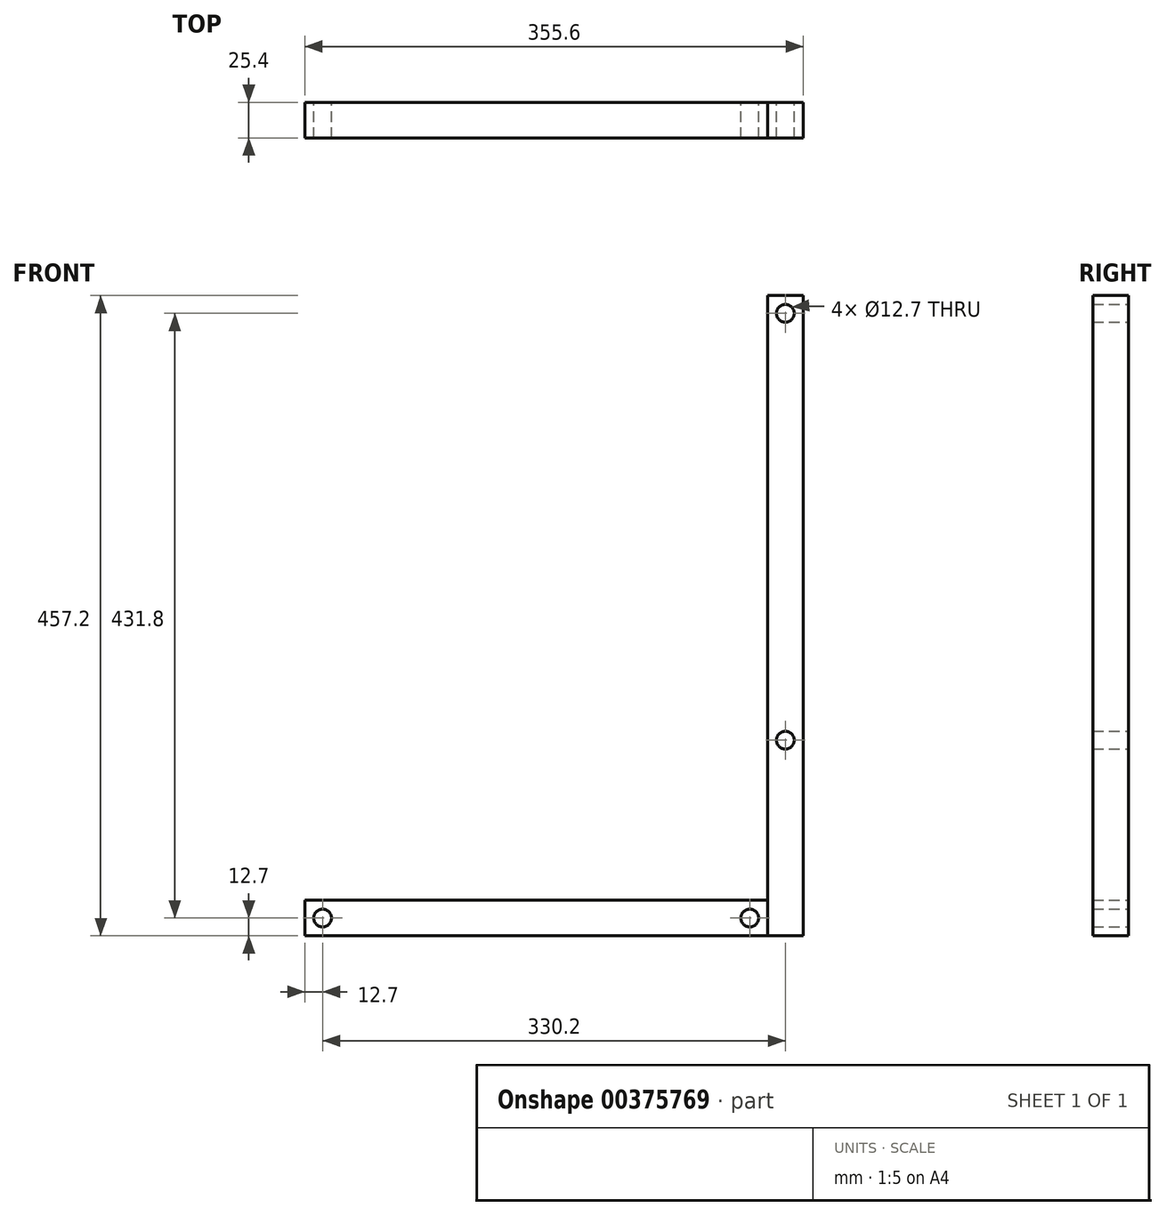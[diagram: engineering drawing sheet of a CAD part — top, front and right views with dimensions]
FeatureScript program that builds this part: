
annotation { "Feature Type Name" : "Feature", "Feature Type Description" : "" }
export const myFeature = defineFeature(function(context is Context, id is Id, definition is map)
    precondition{}
    {
        {
            var Q0;
            Q0=qCreatedBy(makeId("Front.planeOp"),FACE);
            var sketch = newSketch(context, id + "F0", { "sketchPlane" : qUnion([Q0])});
            skLineSegment(sketch, "E0.bottom", {"start": v(0, 457.2) * mm, "end": v(25.4, 457.2) * mm});
            skLineSegment(sketch, "E0.top", {"start": v(0, 0) * mm, "end": v(25.4, 0) * mm});
            skLineSegment(sketch, "E0.left", {"start": v(0, 457.2) * mm, "end": v(0, 0) * mm});
            skLineSegment(sketch, "E0.right", {"start": v(25.4, 457.2) * mm, "end": v(25.4, 0) * mm});
            skCircle(sketch, "E1", {"center": v(12.7, 444.5) * mm, "radius": 6.35 * mm});
            skCircle(sketch, "E2", {"center": v(12.7, 139.7) * mm, "radius": 6.35 * mm});
            skSolve(sketch);
        }
        {
            var Q0;
            Q0=makeQuery(id+"F0.imprint","IMPRINT",FACE,{"disambiguationData":[TD([[makeQuery(id+"F0.imprint","IMPRINT",EDGE,{"derivedFrom":sQuery(id+"F0.wireOp",EDGE,"E0.bottom")}),-1.0]])]});
            extrude(context, id + "F1", {"entities" : qUnion([Q0]), "depth" : 25.4 * mm});
        }
        {
            var Q0;
            Q0=qCreatedBy(makeId("Front.planeOp"),FACE);
            var sketch = newSketch(context, id + "F2", { "sketchPlane" : qUnion([Q0])});
            skLineSegment(sketch, "E3.bottom", {"start": v(0, 0) * mm, "end": v(-330.2, 0) * mm});
            skLineSegment(sketch, "E3.top", {"start": v(0, 25.4) * mm, "end": v(-330.2, 25.4) * mm});
            skLineSegment(sketch, "E3.left", {"start": v(0, 0) * mm, "end": v(0, 25.4) * mm});
            skLineSegment(sketch, "E3.right", {"start": v(-330.2, 0) * mm, "end": v(-330.2, 25.4) * mm});
            skCircle(sketch, "E4", {"center": v(-317.5, 12.7) * mm, "radius": 6.35 * mm});
            skCircle(sketch, "E5", {"center": v(-12.7, 12.7) * mm, "radius": 6.35 * mm});
            skSolve(sketch);
        }
        {
            var Q0;
            Q0=makeQuery(id+"F2.imprint","IMPRINT",FACE,{"disambiguationData":[TD([[makeQuery(id+"F2.imprint","IMPRINT",EDGE,{"derivedFrom":sQuery(id+"F2.wireOp",EDGE,"E3.bottom")}),-1.0]])]});
            extrude(context, id + "F3", {"entities" : qUnion([Q0]), "depth" : 25.4 * mm});
        }
    });
